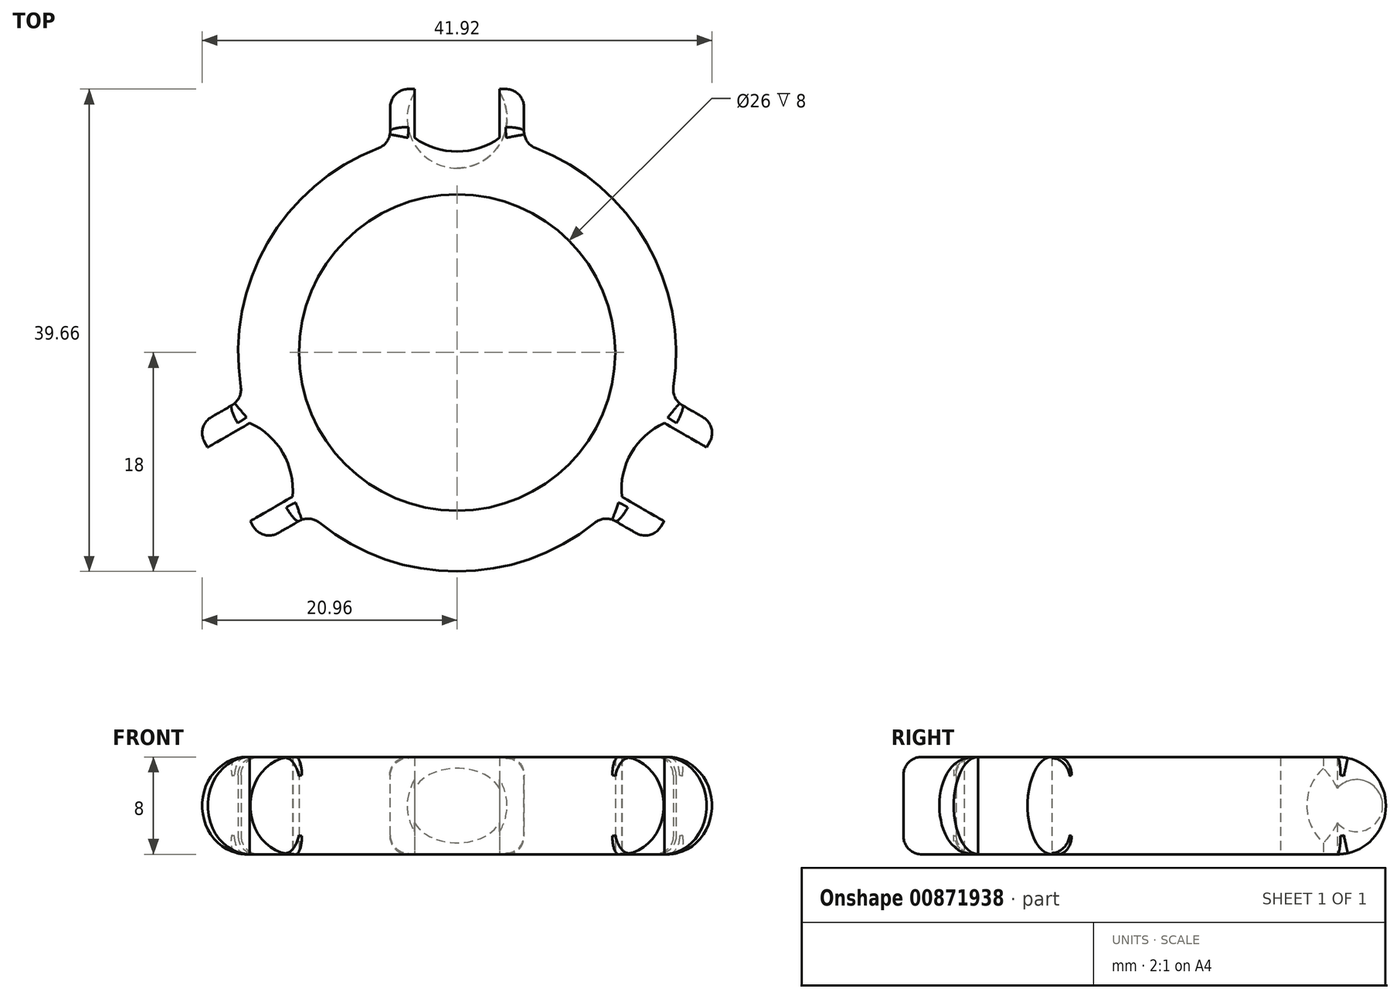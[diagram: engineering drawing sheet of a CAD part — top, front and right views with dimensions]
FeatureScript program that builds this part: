
annotation { "Feature Type Name" : "Feature", "Feature Type Description" : "" }
export const myFeature = defineFeature(function(context is Context, id is Id, definition is map)
    precondition{}
    {
        {
            var Q0;
            Q0=qCreatedBy(makeId("Top.planeOp"),FACE);
            var sketch = newSketch(context, id + "F0", { "sketchPlane" : qUnion([Q0])});
            skArc(sketch, "E0", {"start": v(-5.5, 17.14) * mm, "mid": v(-15.59, 9) * mm, "end": v(-17.6, -3.8) * mm});
            skLineSegment(sketch, "E1", {"start": v(0, 23.66) * mm, "end": v(0, -22.84) * mm, "construction": true});
            skLineSegment(sketch, "E2", {"start": v(-22.74, 0) * mm, "end": v(26.82, 0) * mm, "construction": true});
            skLineSegment(sketch, "E3", {"start": v(-3.5, 17.66) * mm, "end": v(-3.5, 21.66) * mm});
            skLineSegment(sketch, "E4", {"start": v(-3.5, 21.66) * mm, "end": v(-5.5, 21.66) * mm});
            skLineSegment(sketch, "E5", {"start": v(-5.5, 21.66) * mm, "end": v(-5.5, 17.14) * mm});
            skLineSegment(sketch, "E6.MirrorCS", {"start": v(3.5, 17.66) * mm, "end": v(3.5, 21.66) * mm});
            skLineSegment(sketch, "E7.MirrorCS", {"start": v(3.5, 21.66) * mm, "end": v(5.5, 21.66) * mm});
            skLineSegment(sketch, "E8.MirrorCS", {"start": v(5.5, 21.66) * mm, "end": v(5.5, 17.14) * mm});
            skLineSegment(sketch, "E9", {"start": v(-3.5, 17.66) * mm, "end": v(3.5, 17.66) * mm, "construction": true});
            skLineSegment(sketch, "E10", {"start": v(-3.5, 21.66) * mm, "end": v(3.5, 21.66) * mm, "construction": true});
            skPoint(sketch, "E11", {"position": v(0, 9.18) * mm});
            skLineSegment(sketch, "E12.1.0", {"start": v(-16, -15.6) * mm, "end": v(-12.1, -13.33) * mm});
            skLineSegment(sketch, "E12.1.1", {"start": v(-17, -13.86) * mm, "end": v(-16, -15.6) * mm});
            skLineSegment(sketch, "E12.1.2", {"start": v(-17.04, -5.8) * mm, "end": v(-20.5, -7.8) * mm});
            skLineSegment(sketch, "E12.1.3", {"start": v(-20.5, -7.8) * mm, "end": v(-21.5, -6.07) * mm});
            skLineSegment(sketch, "E12.1.4", {"start": v(-21.5, -6.07) * mm, "end": v(-17.6, -3.8) * mm});
            skLineSegment(sketch, "E12.1.5", {"start": v(-13.54, -11.86) * mm, "end": v(-17, -13.86) * mm});
            skLineSegment(sketch, "E12.2.0", {"start": v(21.5, -6.07) * mm, "end": v(17.6, -3.8) * mm});
            skLineSegment(sketch, "E12.2.1", {"start": v(20.5, -7.8) * mm, "end": v(21.5, -6.07) * mm});
            skLineSegment(sketch, "E12.2.2", {"start": v(13.54, -11.86) * mm, "end": v(17, -13.86) * mm});
            skLineSegment(sketch, "E12.2.3", {"start": v(17, -13.86) * mm, "end": v(16, -15.6) * mm});
            skLineSegment(sketch, "E12.2.4", {"start": v(16, -15.6) * mm, "end": v(12.1, -13.33) * mm});
            skLineSegment(sketch, "E12.2.5", {"start": v(17.04, -5.8) * mm, "end": v(20.5, -7.8) * mm});
            skArc(sketch, "E13.trimOffspring", {"start": v(17.6, -3.8) * mm, "mid": v(15.59, 9) * mm, "end": v(5.5, 17.14) * mm});
            skArc(sketch, "E14.trimOffspring", {"start": v(-12.1, -13.33) * mm, "mid": v(0, -18) * mm, "end": v(12.1, -13.33) * mm});
            skCircle(sketch, "E15", {"center": v(0, 0) * mm, "radius": 13 * mm});
            skArc(sketch, "E16", {"start": v(-3.5, 17.66) * mm, "mid": v(0, 16.53) * mm, "end": v(3.5, 17.66) * mm});
            skArc(sketch, "E17.1.0", {"start": v(-13.54, -11.86) * mm, "mid": v(-14.32, -8.26) * mm, "end": v(-17.04, -5.8) * mm});
            skArc(sketch, "E17.2.0", {"start": v(17.04, -5.8) * mm, "mid": v(14.32, -8.26) * mm, "end": v(13.54, -11.86) * mm});
            skSolve(sketch);
        }
        {
            var Q0;
            Q0=qCreatedBy(makeId("Front.planeOp"),FACE);
            var sketch = newSketch(context, id + "F1", { "sketchPlane" : qUnion([Q0])});
            skLineSegment(sketch, "E18", {"start": v(0, -15.32) * mm, "end": v(0, 34.97) * mm, "construction": true});
            skSolve(sketch);
        }
        {
            var Q0;
            Q0 = qSketchRegion(id + "F0", true);
            extrude(context, id + "F2", {"entities" : qUnion([Q0]), "depth" : 8 * mm, "offsetDistance" : 25 * mm});
        }
        {
            var Q0;
            Q0=qCreatedBy(makeId("Top.planeOp"),FACE);
            cPlane(context, id + "F3", {"entities" : qUnion([Q0]), "cplaneType" : CPlaneType.OFFSET, "offset" : 4 * mm, "width" : 150 * mm, "height" : 150 * mm});
        }
        {
            var Q0;
            Q0=qCreatedBy(id+"F3.planeOp",FACE);
            var sketch = newSketch(context, id + "F4", { "sketchPlane" : qUnion([Q0])});
            skPoint(sketch, "E19.0", {"position": v(-3.5, 21.66) * mm});
            skPoint(sketch, "E20.0", {"position": v(3.5, 21.66) * mm});
            skLineSegment(sketch, "E21", {"start": v(0, 23.36) * mm, "end": v(0, 15.16) * mm});
            skArc(sketch, "E22", {"start": v(0, 23.36) * mm, "mid": v(-4.1, 19.26) * mm, "end": v(0, 15.16) * mm});
            skLineSegment(sketch, "E23", {"start": v(-3.5, 21.66) * mm, "end": v(3.5, 21.66) * mm, "construction": true});
            skLineSegment(sketch, "E24", {"start": v(0, 27.74) * mm, "end": v(0, 23.36) * mm, "construction": true});
            skPoint(sketch, "E25", {"position": v(0, 23.36) * mm});
            skSolve(sketch);
        }
        {
            var Q0;
            Q0 = qSketchRegion(id + "F4", true);
            var Q1;
            Q1=sQuery(id+"F4.wireOp",EDGE,"E21");
            revolve(context, id + "F5", {"operationType" : NewBodyOperationType.REMOVE, "surfaceOperationType" : NewSurfaceOperationType.NEW, "entities" : qUnion([Q0]), "axis" : qUnion([Q1]), "revolveType" : RevolveType.FULL, "oppositeDirection" : true});
        }
        {
            var Q0;
            Q0=makeQuery(id+"F2.opExtrude","CAP_EDGE",EDGE,{"disambiguationData":[OSD([sQuery(id+"F0.wireOp",EDGE,"E4")])],"isStart":false});
            var Q1;
            Q1=makeQuery(id+"F2.opExtrude","CAP_EDGE",EDGE,{"disambiguationData":[OSD([sQuery(id+"F0.wireOp",EDGE,"E7.MirrorCS")])],"isStart":false});
            var Q2;
            Q2=makeQuery(id+"F2.opExtrude","CAP_EDGE",EDGE,{"disambiguationData":[OSD([sQuery(id+"F0.wireOp",EDGE,"E12.2.1")])],"isStart":false});
            var Q3;
            Q3=makeQuery(id+"F2.opExtrude","CAP_EDGE",EDGE,{"disambiguationData":[OSD([sQuery(id+"F0.wireOp",EDGE,"E12.2.3")])],"isStart":false});
            var Q4;
            Q4=makeQuery(id+"F2.opExtrude","CAP_EDGE",EDGE,{"disambiguationData":[OSD([sQuery(id+"F0.wireOp",EDGE,"E12.1.1")])],"isStart":false});
            var Q5;
            Q5=makeQuery(id+"F2.opExtrude","CAP_EDGE",EDGE,{"disambiguationData":[OSD([sQuery(id+"F0.wireOp",EDGE,"E12.1.3")])],"isStart":false});
            var Q6;
            Q6=makeQuery(id+"F2.opExtrude","CAP_EDGE",EDGE,{"disambiguationData":[OSD([sQuery(id+"F0.wireOp",EDGE,"E12.1.1")])],"isStart":true});
            var Q7;
            Q7=makeQuery(id+"F2.opExtrude","CAP_EDGE",EDGE,{"disambiguationData":[OSD([sQuery(id+"F0.wireOp",EDGE,"E12.1.3")])],"isStart":true});
            var Q8;
            Q8=makeQuery(id+"F2.opExtrude","CAP_EDGE",EDGE,{"disambiguationData":[OSD([sQuery(id+"F0.wireOp",EDGE,"E12.2.3")])],"isStart":true});
            var Q9;
            Q9=makeQuery(id+"F2.opExtrude","CAP_EDGE",EDGE,{"disambiguationData":[OSD([sQuery(id+"F0.wireOp",EDGE,"E12.2.1")])],"isStart":true});
            var Q10;
            Q10=makeQuery(id+"F2.opExtrude","CAP_EDGE",EDGE,{"disambiguationData":[OSD([sQuery(id+"F0.wireOp",EDGE,"E7.MirrorCS")])],"isStart":true});
            var Q11;
            Q11=makeQuery(id+"F2.opExtrude","CAP_EDGE",EDGE,{"disambiguationData":[OSD([sQuery(id+"F0.wireOp",EDGE,"E4")])],"isStart":true});
            fillet(context, id + "F6", {"entities" : qUnion([Q0, Q1, Q2, Q3, Q4, Q5, Q6, Q7, Q8, Q9, Q10, Q11]), "radius" : 4 * mm, "tangentPropagation" : true, "allowEdgeOverflow" : false});
        }
        {
            var Q0;
            Q0=makeQuery(id+"F2.opExtrude","SWEPT_EDGE",EDGE,{"disambiguationData":[OSD([sQuery(id+"F0.wireOp",EDGE,"E0"),sQuery(id+"F0.wireOp",EDGE,"E12.1.4")])]});
            var Q1;
            Q1=makeQuery(id+"F2.opExtrude","SWEPT_EDGE",EDGE,{"disambiguationData":[OSD([sQuery(id+"F0.wireOp",EDGE,"E0"),sQuery(id+"F0.wireOp",EDGE,"E5")])]});
            var Q2;
            Q2=makeQuery(id+"F2.opExtrude","SWEPT_EDGE",EDGE,{"disambiguationData":[OSD([sQuery(id+"F0.wireOp",EDGE,"E8.MirrorCS"),sQuery(id+"F0.wireOp",EDGE,"E13.trimOffspring")])]});
            var Q3;
            Q3=makeQuery(id+"F2.opExtrude","SWEPT_EDGE",EDGE,{"disambiguationData":[OSD([sQuery(id+"F0.wireOp",EDGE,"E12.2.0"),sQuery(id+"F0.wireOp",EDGE,"E13.trimOffspring")])]});
            var Q4;
            Q4=makeQuery(id+"F2.opExtrude","SWEPT_EDGE",EDGE,{"disambiguationData":[OSD([sQuery(id+"F0.wireOp",EDGE,"E12.2.4"),sQuery(id+"F0.wireOp",EDGE,"E14.trimOffspring")])]});
            var Q5;
            Q5=makeQuery(id+"F2.opExtrude","SWEPT_EDGE",EDGE,{"disambiguationData":[OSD([sQuery(id+"F0.wireOp",EDGE,"E12.1.0"),sQuery(id+"F0.wireOp",EDGE,"E14.trimOffspring")])]});
            fillet(context, id + "F7", {"entities" : qUnion([Q0, Q1, Q2, Q3, Q4, Q5]), "radius" : 1.5 * mm, "tangentPropagation" : true, "allowEdgeOverflow" : false});
        }
        {
            var Q0;
            Q0=makeQuery(id+"F2.opExtrude","CAP_EDGE",EDGE,{"disambiguationData":[OSD([sQuery(id+"F0.wireOp",EDGE,"E0")])],"isStart":true});
            var Q1;
            Q1=makeQuery(id+"F2.opExtrude","CAP_EDGE",EDGE,{"disambiguationData":[OSD([sQuery(id+"F0.wireOp",EDGE,"E14.trimOffspring")])],"isStart":true});
            var Q2;
            Q2=makeQuery(id+"F2.opExtrude","CAP_EDGE",EDGE,{"disambiguationData":[OSD([sQuery(id+"F0.wireOp",EDGE,"E13.trimOffspring")])],"isStart":true});
            fillet(context, id + "F8", {"entities" : qUnion([Q0, Q1, Q2]), "radius" : 1.5 * mm, "tangentPropagation" : true, "allowEdgeOverflow" : false});
        }
    });
